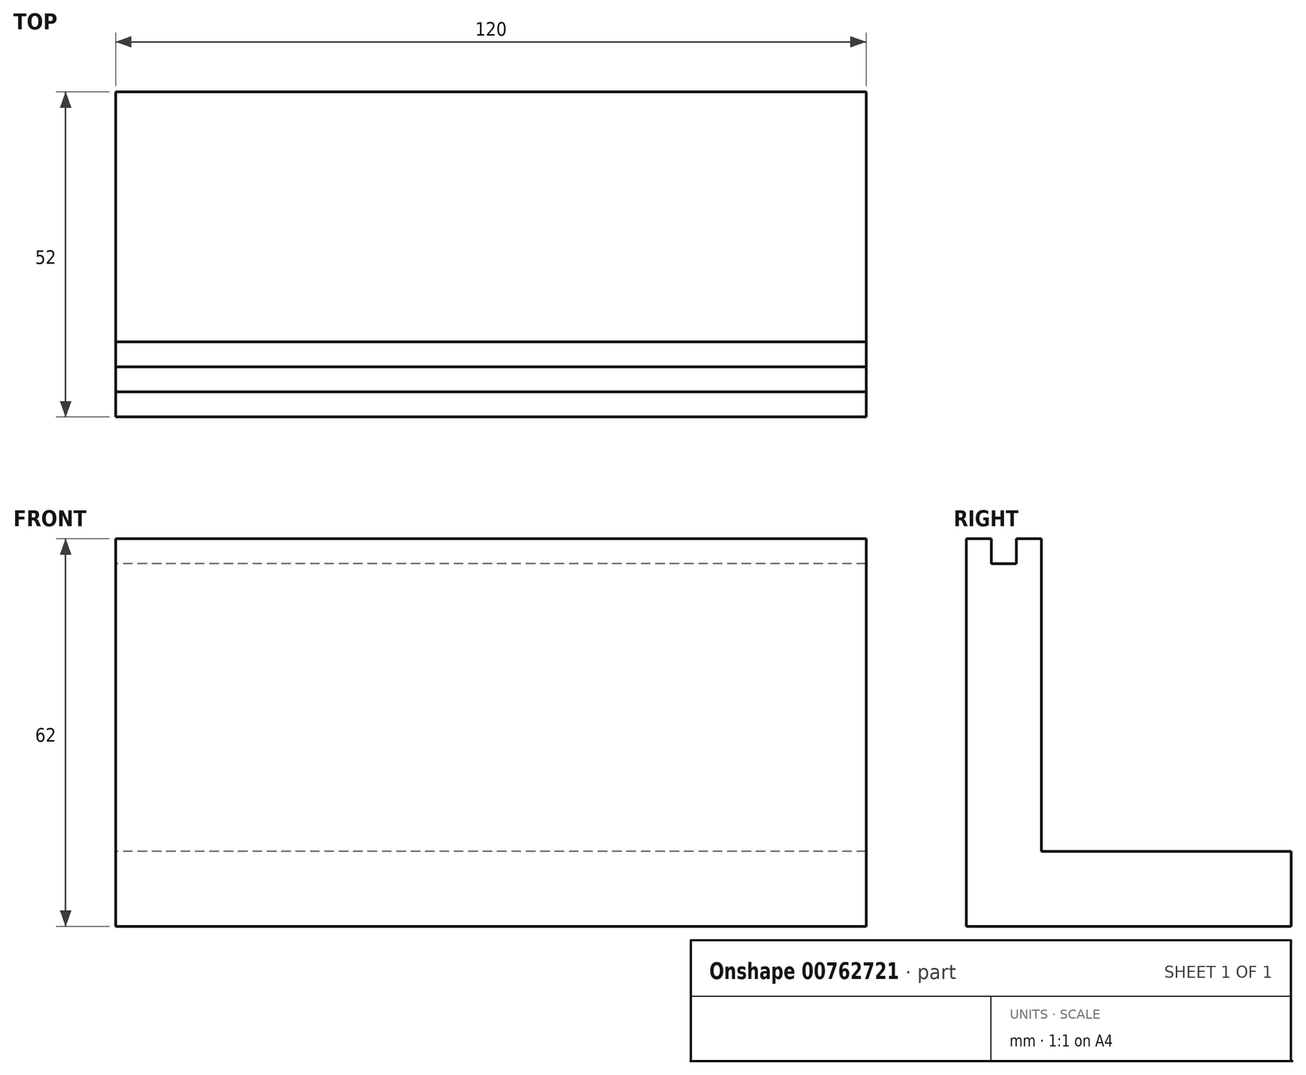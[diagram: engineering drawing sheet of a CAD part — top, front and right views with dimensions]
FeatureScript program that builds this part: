
annotation { "Feature Type Name" : "Feature", "Feature Type Description" : "" }
export const myFeature = defineFeature(function(context is Context, id is Id, definition is map)
    precondition{}
    {
        {
            var Q0;
            Q0=qCreatedBy(makeId("Right.planeOp"),FACE);
            var sketch = newSketch(context, id + "F0", { "sketchPlane" : qUnion([Q0])});
            skLineSegment(sketch, "E0", {"start": v(0, 0) * mm, "end": v(0, 62) * mm});
            skLineSegment(sketch, "E1", {"start": v(0, 62) * mm, "end": v(4, 62) * mm});
            skLineSegment(sketch, "E2", {"start": v(12, 62) * mm, "end": v(12, 12) * mm});
            skLineSegment(sketch, "E3", {"start": v(12, 12) * mm, "end": v(52, 12) * mm});
            skLineSegment(sketch, "E4", {"start": v(52, 12) * mm, "end": v(52, 0) * mm});
            skLineSegment(sketch, "E5", {"start": v(52, 0) * mm, "end": v(0, 0) * mm});
            skLineSegment(sketch, "E6.bottom", {"start": v(8, 58) * mm, "end": v(4, 58) * mm});
            skLineSegment(sketch, "E6.left", {"start": v(8, 58) * mm, "end": v(8, 62) * mm});
            skLineSegment(sketch, "E6.right", {"start": v(4, 58) * mm, "end": v(4, 62) * mm});
            skPoint(sketch, "E6.middle", {"position": v(6, 62) * mm});
            skPoint(sketch, "E6.top.end.orphan", {"position": v(4, 66) * mm});
            skPoint(sketch, "E7.orphan", {"position": v(8, 66) * mm});
            skLineSegment(sketch, "E8.trimOffspring", {"start": v(8, 62) * mm, "end": v(12, 62) * mm});
            skSolve(sketch);
        }
        {
            var Q0;
            Q0=makeQuery(id+"F0.imprint","IMPRINT",FACE,{"disambiguationData":[TD([[makeQuery(id+"F0.imprint","IMPRINT",EDGE,{"derivedFrom":sQuery(id+"F0.wireOp",EDGE,"E0")}),-1.0]])]});
            extrude(context, id + "F1", {"entities" : qUnion([Q0]), "endBound" : BoundingType.SYMMETRIC, "depth" : 120 * mm, "offsetDistance" : 25 * mm});
        }
    });
